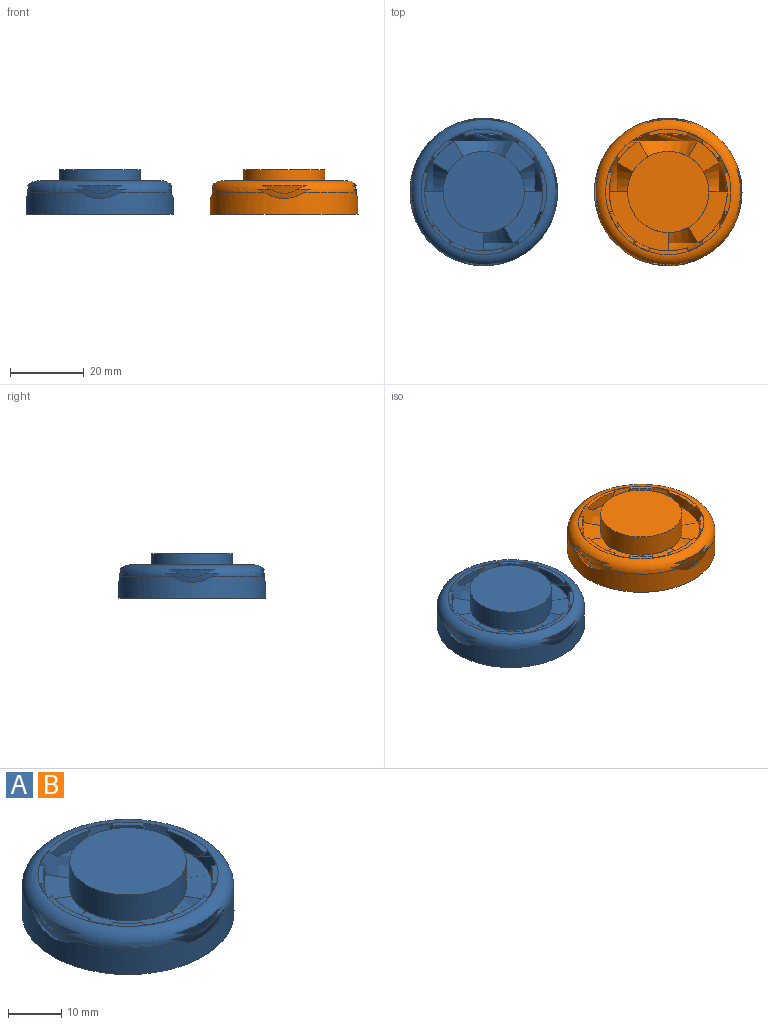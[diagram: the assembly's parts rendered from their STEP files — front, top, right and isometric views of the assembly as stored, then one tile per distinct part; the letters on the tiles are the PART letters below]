
ASSEMBLY  parts=2 mates=1
PART A: 72 faces, bbox 43.6x43.6x28.3 mm
  f0: torus R=17mm, axis (0,0,1), area 482.5mm2, adj f1,f2,f3,f10,f58,f59,f60,f61
  f1: revolved ~14.25x6.67mm, area 32.1mm2, adj f0,f62,f68
  f2: revolved ~14.25x6.67mm, area 32.1mm2, adj f0,f63,f65
  f3: cylinder r=20mm len=40mm, axis (0,0,-1), area 701.6mm2, adj f0,f18,f59,f60,f62,f63
  f4: cylinder r=16mm len=5.86mm, axis (0,0,1), area 20.9mm2, adj f10,f12,f41,f55
  f5: cylinder r=16mm len=5.86mm, axis (0,0,1), area 20.9mm2, adj f6,f10,f33,f53
  f6: plane 8.7x8.7mm, normal (0,0,1), area 35.3mm2, adj f5,f16,f29,f50
  f7: cylinder r=16mm len=19.05mm, axis (0,0,1), area 43.9mm2, adj f10,f11,f24,f31,f32,f44,f45,f47
  f8: cylinder r=16mm len=10.39mm, axis (0,0,1), area 22.4mm2, adj f10,f12,f52,f54,f57
  f9: cylinder r=16mm len=10.39mm, axis (0,0,1), area 22.4mm2, adj f10,f12,f37,f40,f42
  f10: plane 34.01x34.01mm, normal (0,0,1), area 72.9mm2, adj f0,f4,f5,f7,f8,f9,f14,f15
  f11: plane 8.7x8.7mm, normal (0,0,1), area 35.3mm2, adj f7,f16,f21,f29
  f12: plane 16.07x16.07mm, normal (0,0,1), area 106.6mm2, adj f4,f8,f9,f16,f34,f43,f48,f56
  f13: plane 14.25x10.84mm, normal (0,0,1), area 70.9mm2, adj f14,f15,f16,f19,f27,f36
  f14: cylinder r=16mm len=5.86mm, axis (0,0,1), area 20.9mm2, adj f10,f13,f26,f39
  f15: cylinder r=16mm len=10.39mm, axis (0,0,1), area 22.4mm2, adj f10,f13,f22,f23,f28
  f16: cylinder r=11mm len=22mm, axis (0,0,-1), area 414.7mm2, adj f6,f11,f12,f13,f17,f20,f30,f35
  f17: plane 22x22mm, normal (0,0,1), area 380.1mm2, adj f16
  f18: plane 40x40mm, normal (0,0,-1), area 1256.6mm2, adj f3
  f19: plane 7.97x6.49mm, normal (0,0.02,-1), area 35.1mm2, adj f13,f20,f21,f25
  f20: bspline ~22.89x22.83mm, area 19.6mm2, adj f16,f19,f21
  f21: revolved ~15.89x6.4mm, area 70.8mm2, adj f11,f19,f20,f25
  f22: plane 0.05x0mm, normal (0,0.02,-1), area 0mm2, adj f15,f23,f25
  f23: cylinder r=6mm len=5.09mm, axis (1,0,0), area 2.1mm2, adj f10,f15,f22,f25
  f24: revolved ~3.35x1.66mm, area 1.4mm2, adj f7,f10,f25
  f25: bspline ~27.89x27.88mm, area 68.7mm2, adj f10,f19,f21,f22,f23,f24
  f26: revolved ~3.15x2.02mm, area 1.4mm2, adj f10,f14,f27
  f27: bspline ~10x9.93mm, area 17.7mm2, adj f10,f13,f26,f28
  f28: cylinder r=6mm len=5.2mm, axis (1,0,0), area 2.7mm2, adj f10,f15,f27
  f29: revolved ~16x6.4mm, area 71.5mm2, adj f6,f11,f30,f32
  f30: bspline ~22.9x22.85mm, area 20mm2, adj f16,f29
  f31: cylinder r=6mm len=5.2mm, axis (0,-1,0), area 2.7mm2, adj f7,f10,f32
  f32: bspline ~27.86x27.81mm, area 69.4mm2, adj f7,f10,f29,f31,f33
  f33: revolved ~3.35x1.66mm, area 1.4mm2, adj f5,f10,f32
  f34: plane 7.97x6.49mm, normal (0.02,0,-1), area 35.1mm2, adj f12,f35,f36,f38
  f35: bspline ~22.89x22.83mm, area 19.6mm2, adj f16,f34,f36
  f36: revolved ~15.89x6.4mm, area 70.8mm2, adj f13,f34,f35,f38
  f37: cylinder r=6mm len=5.09mm, axis (0,-1,0), area 2.1mm2, adj f9,f10,f38,f40
  f38: bspline ~27.89x27.88mm, area 68.7mm2, adj f10,f34,f36,f37,f39,f40
  f39: revolved ~3.35x1.66mm, area 1.4mm2, adj f10,f14,f38
  f40: plane 0.05x0mm, normal (0.02,0,-1), area 0mm2, adj f9,f37,f38
  f41: revolved ~3.15x2.02mm, area 1.4mm2, adj f4,f10,f43
  f42: cylinder r=6mm len=5.2mm, axis (0,-1,0), area 2.7mm2, adj f9,f10,f43
  f43: bspline ~10x9.93mm, area 17.7mm2, adj f10,f12,f41,f42
  f44: plane 8.02x2.21mm, normal (-0.02,0,1), area 0.2mm2, adj f7,f45,f46,f47
  f45: revolved ~3.02x1.92mm, area 1.5mm2, adj f7,f10,f44,f46
  f46: bspline ~9.93x9.9mm, area 17mm2, adj f10,f44,f45,f47
  f47: cylinder r=6mm len=5.09mm, axis (0,-1,0), area 2.1mm2, adj f7,f10,f44,f46
  f48: plane 7.97x6.49mm, normal (0,0.02,-1), area 35.1mm2, adj f12,f49,f50,f51
  f49: bspline ~22.89x22.83mm, area 19.6mm2, adj f16,f48,f50
  f50: revolved ~15.89x6.4mm, area 70.8mm2, adj f6,f48,f49,f51
  f51: bspline ~27.89x27.88mm, area 68.8mm2, adj f10,f48,f50,f52,f53,f54
  f52: cylinder r=6mm len=5.09mm, axis (1,0,0), area 2.1mm2, adj f8,f10,f51,f54
  f53: revolved ~3.35x1.66mm, area 1.4mm2, adj f5,f10,f51
  f54: plane 0.05x0mm, normal (0,0.02,-1), area 0mm2, adj f8,f51,f52
  f55: revolved ~3.15x2.02mm, area 1.4mm2, adj f4,f10,f56
  f56: bspline ~10x9.93mm, area 17.6mm2, adj f10,f12,f55,f57
  f57: cylinder r=6mm len=5.2mm, axis (1,0,0), area 2.7mm2, adj f8,f10,f56
  f58: revolved ~14.25x6.67mm, area 32.1mm2, adj f0,f59,f67
  f59: revolved ~14.25x4.87mm, area 20.3mm2, adj f0,f3,f58
  f60: revolved ~14.25x4.87mm, area 20.3mm2, adj f0,f3,f61
  f61: revolved ~14.25x6.67mm, area 32.1mm2, adj f0,f60,f70
  f62: revolved ~14.25x4.87mm, area 20.3mm2, adj f0,f1,f3
  f63: revolved ~14.25x4.87mm, area 20.3mm2, adj f0,f2,f3
  f64: sphere r=20mm, area 26.9mm2, adj f0,f65
  f65: revolved ~11.98x3.67mm, area 15.5mm2, adj f0,f2,f64
  f66: sphere r=20mm, area 26.9mm2, adj f0,f67
  f67: revolved ~11.98x3.67mm, area 15.5mm2, adj f0,f58,f66
  f68: revolved ~11.98x3.67mm, area 15.5mm2, adj f0,f1,f69
  f69: sphere r=20mm, area 26.9mm2, adj f0,f68
  f70: revolved ~11.98x3.67mm, area 15.5mm2, adj f0,f61,f71
  f71: sphere r=20mm, area 26.9mm2, adj f0,f70
PART B: same geometry as A
PLACE A t=(-90,0,-5.12)mm
PLACE B t=(-40,0,-5.12)mm
MATE planar B.f0 <-> A.f0  axis (0,0,-1) through (-40,0,-5.12)mm
